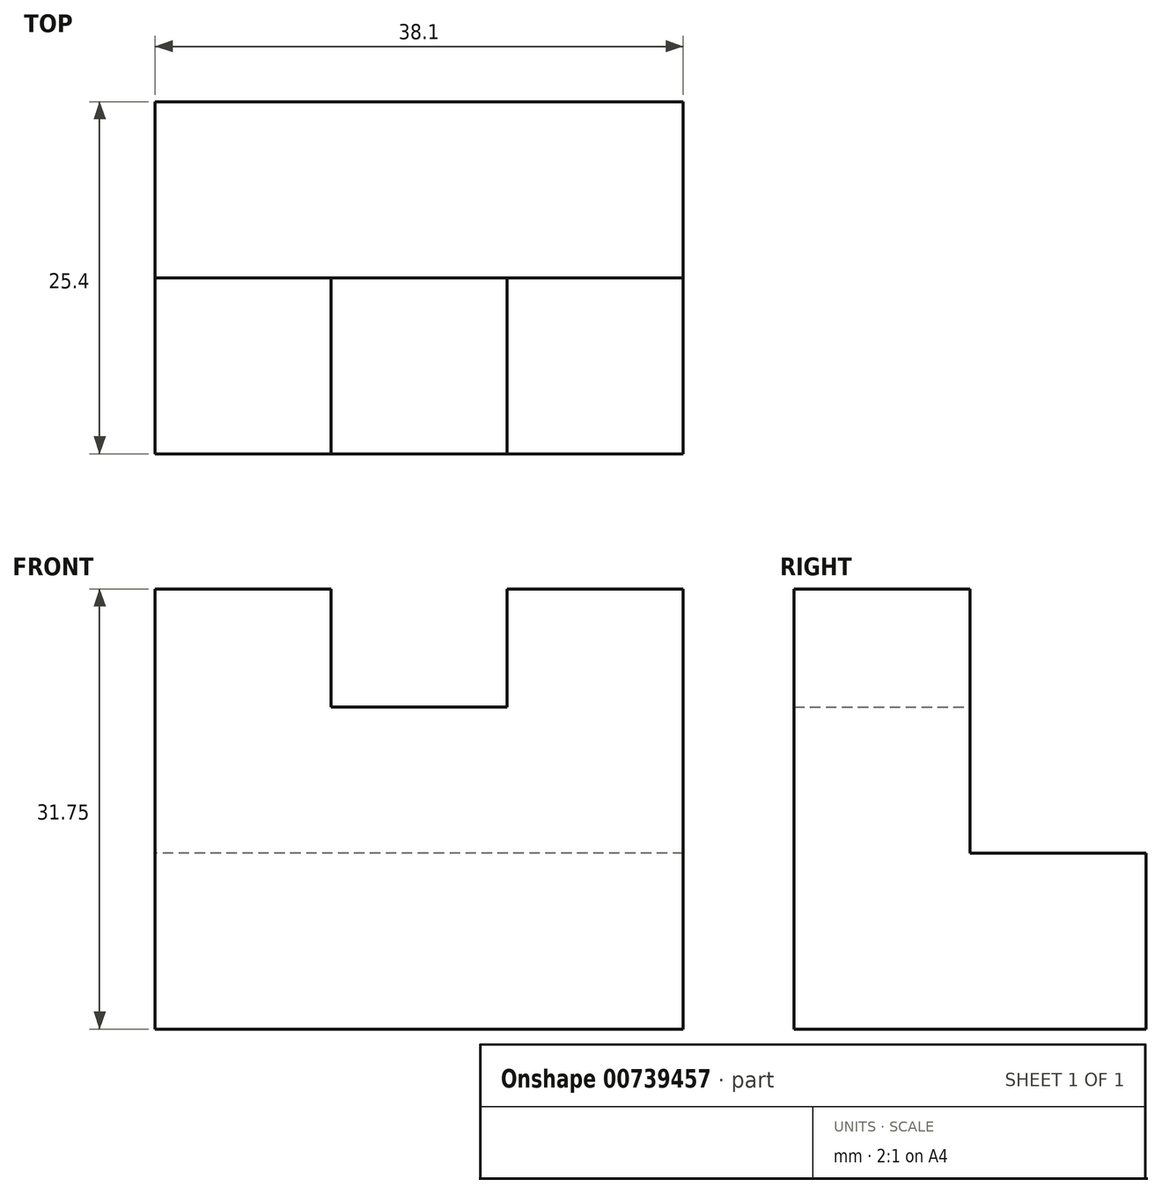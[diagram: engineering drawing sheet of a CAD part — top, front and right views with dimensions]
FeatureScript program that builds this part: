
annotation { "Feature Type Name" : "Feature", "Feature Type Description" : "" }
export const myFeature = defineFeature(function(context is Context, id is Id, definition is map)
    precondition{}
    {
        {
            var Q0;
            Q0=qCreatedBy(makeId("Front.planeOp"),FACE);
            var sketch = newSketch(context, id + "F0", { "sketchPlane" : qUnion([Q0])});
            skLineSegment(sketch, "E0", {"start": v(0, 0) * mm, "end": v(38.1, 0) * mm});
            skLineSegment(sketch, "E1", {"start": v(38.1, 0) * mm, "end": v(38.1, 31.75) * mm});
            skLineSegment(sketch, "E2", {"start": v(38.1, 31.75) * mm, "end": v(25.4, 31.75) * mm});
            skLineSegment(sketch, "E3", {"start": v(25.4, 31.75) * mm, "end": v(25.4, 23.23) * mm});
            skLineSegment(sketch, "E4", {"start": v(25.4, 23.23) * mm, "end": v(12.7, 23.23) * mm});
            skLineSegment(sketch, "E5", {"start": v(12.7, 23.23) * mm, "end": v(12.7, 31.75) * mm});
            skLineSegment(sketch, "E6", {"start": v(12.7, 31.75) * mm, "end": v(0, 31.75) * mm});
            skLineSegment(sketch, "E7", {"start": v(0, 31.75) * mm, "end": v(0, 0) * mm});
            skSolve(sketch);
        }
        {
            var Q0;
            Q0=makeQuery(id+"F0.imprint","IMPRINT",FACE,{"disambiguationData":[TD([[makeQuery(id+"F0.imprint","IMPRINT",EDGE,{"derivedFrom":sQuery(id+"F0.wireOp",EDGE,"E0")}),1.0]])]});
            extrude(context, id + "F1", {"entities" : qUnion([Q0]), "depth" : 12.7 * mm, "offsetDistance" : 25.4 * mm});
        }
        {
            var Q0;
            Q0=makeQuery(id+"F1.opExtrude","CAP_FACE",FACE,{"disambiguationData":[OSD([sQuery(id+"F0.wireOp",EDGE,"E0"),sQuery(id+"F0.wireOp",EDGE,"E1"),sQuery(id+"F0.wireOp",EDGE,"E2"),sQuery(id+"F0.wireOp",EDGE,"E3"),sQuery(id+"F0.wireOp",EDGE,"E4"),sQuery(id+"F0.wireOp",EDGE,"E5"),sQuery(id+"F0.wireOp",EDGE,"E6"),sQuery(id+"F0.wireOp",EDGE,"E7")])],"isStart":true});
            var sketch = newSketch(context, id + "F2", { "sketchPlane" : qUnion([Q0])});
            skLineSegment(sketch, "E8", {"start": v(-38.1, 0) * mm, "end": v(-38.1, 12.7) * mm});
            skLineSegment(sketch, "E9", {"start": v(-38.1, 12.7) * mm, "end": v(0, 12.7) * mm});
            skLineSegment(sketch, "E10", {"start": v(0, 12.7) * mm, "end": v(0, 0) * mm});
            skSolve(sketch);
        }
        {
            var Q0;
            Q0=makeQuery(id+"F2.imprint","IMPRINT",FACE,{"disambiguationData":[TD([[makeQuery(id+"F2.imprint","IMPRINT",EDGE,{"derivedFrom":sQuery(id+"F2.wireOp",EDGE,"E8")}),-1.0]])]});
            extrude(context, id + "F3", {"entities" : qUnion([Q0]), "operationType" : NewBodyOperationType.ADD, "depth" : 12.7 * mm, "offsetDistance" : 25.4 * mm});
        }
    });
